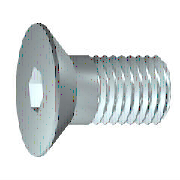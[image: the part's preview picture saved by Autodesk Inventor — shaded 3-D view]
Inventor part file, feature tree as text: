
AUTODESK INVENTOR PART (.ipt)
format: ipt  version: 2020 (Build 240168000, 168)  size: 178,176 bytes
history: native  units: mm (DEFAULTED — no unit token found)
features: sketch x2, extrude x1, plane x1
ambient origin geometry x7: Origin, YZ Plane, XY Plane, X Axis, Y Axis, Z Axis, Center Point
bodies: Solid1 (feature_tree), Body (feature_tree)
feature tree (4):
  sketch  "Sketch2"  dims[d2=1.5mm d3=4.0mm d6=2.48mm d7=45.0deg d8=2.886751mm d9=60.0deg d10=7.53mm d11=4.0mm d12=0.429415mm d13=90.0deg d30=10.0mm d14=0.0mm d15=20.0mm d16=0.0mm d17=0.429415mm d18=0.429415mm d20=0.0mm d39=45.0deg d43=0.0mm d44=0.0mm]
  extrude  "Slot"  Depth=20.0mm
  plane  "Work Plane1"
  sketch  "Sketch1"  dims[d0=45.0mm d1=20.0mm]
